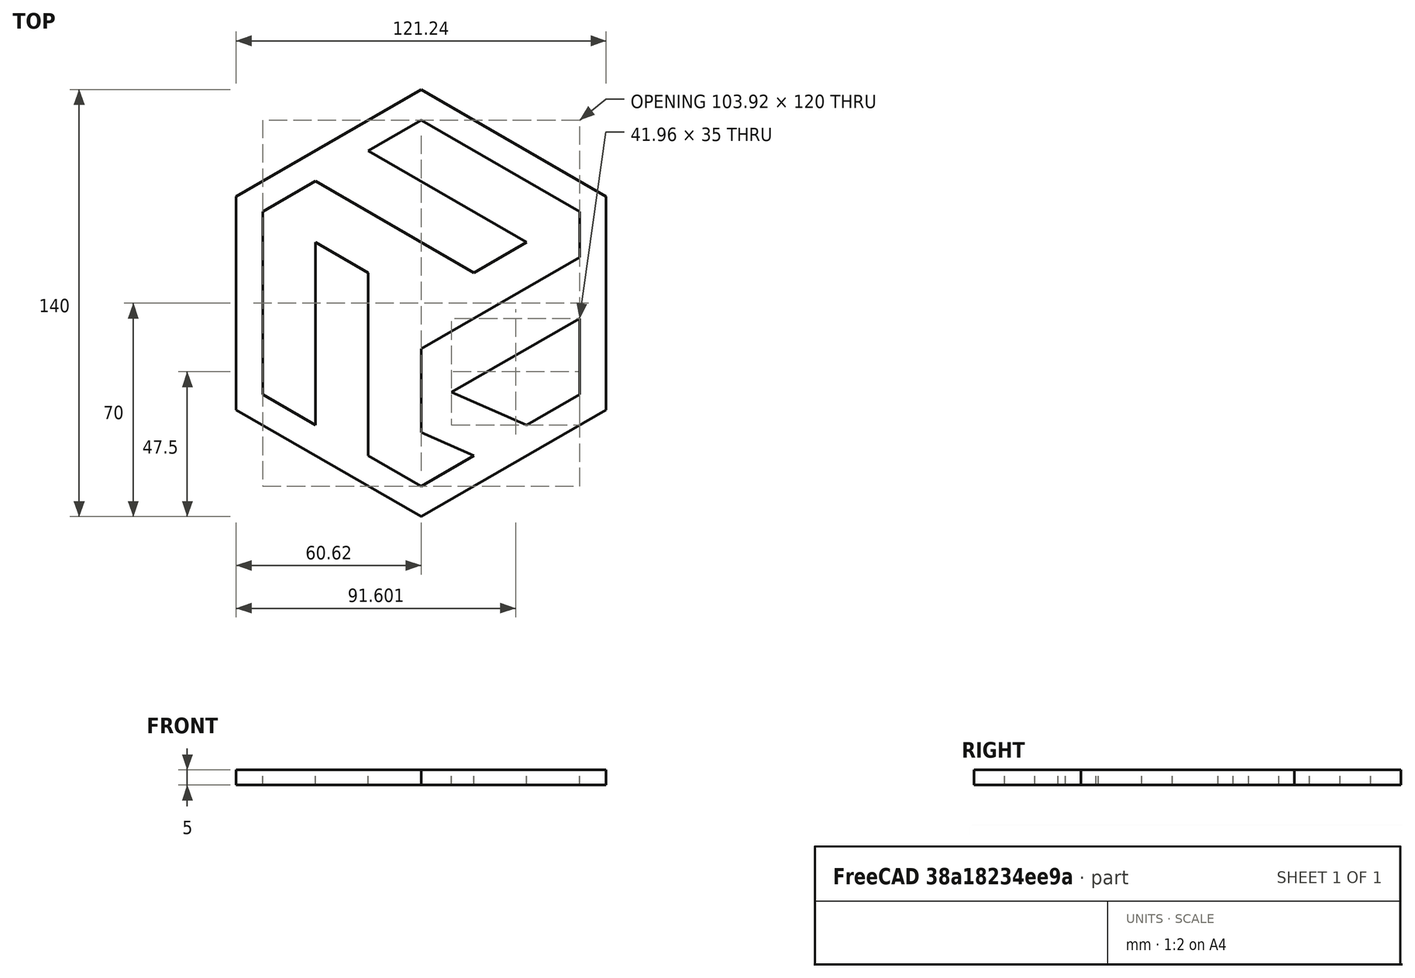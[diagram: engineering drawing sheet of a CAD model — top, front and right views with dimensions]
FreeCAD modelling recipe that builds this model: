
FCSTD DOCUMENT  (FreeCAD 0.20R29603 (Git))
Label: logo
License: All rights reserved
LicenseURL: http://en.wikipedia.org/wiki/All_rights_reserved
objects: Sketcher::SketchObject×1, PartDesign::Pad×1, PartDesign::Body×1
note: 4 computed .brp shape members not serialized (recipe doc carries the construction recipe); baked Part::Feature solids carry a one-line shape summary decoded from their .brp

FEATURE [Sketcher::SketchObject] Sketch
  FullyConstrained = true
  MapMode = 5
  Support = -> [XY_Plane]
  sketch-geometry (37):
    g0: LineSegment StartX=51.9615 StartY=-30 StartZ=0 EndX=51.9615 EndY=30 EndZ=0
    g1: LineSegment StartX=51.9615 StartY=30 StartZ=0 EndX=0 EndY=60 EndZ=0
    g2: LineSegment StartX=0 StartY=60 StartZ=0 EndX=-51.9615 EndY=30 EndZ=0
    g3: LineSegment StartX=-51.9615 StartY=30 StartZ=0 EndX=-51.9615 EndY=-30 EndZ=0
    g4: LineSegment StartX=-51.9615 StartY=-30 StartZ=0 EndX=7.1e-15 EndY=-60 EndZ=0
    g5: LineSegment StartX=5.2e-15 StartY=-60 StartZ=0 EndX=51.9615 EndY=-30 EndZ=0
    g6: Circle CenterX=0 CenterY=-7.1e-15 CenterZ=0 NormalX=0 NormalY=0 NormalZ=1 AngleXU=0 Radius=60
    g7: LineSegment StartX=-17.3205 StartY=50 StartZ=0 EndX=34.641 EndY=20 EndZ=0
    g8: LineSegment StartX=-34.641 StartY=40 StartZ=0 EndX=17.3205 EndY=10 EndZ=0
    g9: LineSegment StartX=17.3205 StartY=10 StartZ=0 EndX=34.641 EndY=20 EndZ=0
    g10: LineSegment StartX=-34.641 StartY=-40 StartZ=0 EndX=-34.641 EndY=20 EndZ=0
    g11: LineSegment StartX=-34.641 StartY=20 StartZ=0 EndX=-17.3205 EndY=10 EndZ=0
    g12: LineSegment StartX=-17.3205 StartY=10 StartZ=0 EndX=-17.3205 EndY=-50 EndZ=0
    g13: LineSegment StartX=51.9615 StartY=15 StartZ=0 EndX=0 EndY=-15 EndZ=0
    g14: LineSegment StartX=51.9615 StartY=-5 StartZ=0 EndX=10 EndY=-29.2265 EndZ=0
    g15: LineSegment StartX=10 StartY=-29.2265 StartZ=0 EndX=34.641 EndY=-40 EndZ=0
    g16: LineSegment StartX=0 StartY=-15 StartZ=0 EndX=0 EndY=-42.4272 EndZ=0
    g17: LineSegment StartX=0 StartY=-42.4272 StartZ=0 EndX=17.3205 EndY=-50 EndZ=0
    g18: LineSegment StartX=-51.9615 StartY=30 StartZ=0 EndX=0 EndY=-7.1e-15 EndZ=0
    g19: LineSegment StartX=51.9615 StartY=30 StartZ=0 EndX=0 EndY=-7.1e-15 EndZ=0
    g20: LineSegment StartX=60.6218 StartY=35 StartZ=0 EndX=-7.1e-15 EndY=70 EndZ=0
    g21: LineSegment StartX=-7.1e-15 StartY=70 StartZ=0 EndX=-60.6218 EndY=35 EndZ=0
    g22: LineSegment StartX=-60.6218 StartY=35 StartZ=0 EndX=-60.6218 EndY=-35 EndZ=0
    g23: LineSegment StartX=-60.6218 StartY=-35 StartZ=0 EndX=0 EndY=-70 EndZ=0
    g24: LineSegment StartX=0 StartY=-70 StartZ=0 EndX=60.6218 EndY=-35 EndZ=0
    g25: LineSegment StartX=60.6218 StartY=-35 StartZ=0 EndX=60.6218 EndY=35 EndZ=0
    g26: Circle CenterX=0 CenterY=-7.1e-15 CenterZ=0 NormalX=0 NormalY=0 NormalZ=1 AngleXU=0 Radius=70
    g27: LineSegment StartX=0 StartY=60 StartZ=0 EndX=-17.3205 EndY=50 EndZ=0
    g28: LineSegment StartX=-34.641 StartY=40 StartZ=0 EndX=-51.9615 EndY=30 EndZ=0
    g29: LineSegment StartX=-51.9615 StartY=30 StartZ=0 EndX=-51.9615 EndY=-30 EndZ=0
    g30: LineSegment StartX=-51.9615 StartY=-30 StartZ=0 EndX=-34.641 EndY=-40 EndZ=0
    g31: LineSegment StartX=-17.3205 StartY=-50 StartZ=0 EndX=3.6e-15 EndY=-60 EndZ=0
    g32: LineSegment StartX=5.2e-15 StartY=-60 StartZ=0 EndX=17.3205 EndY=-50 EndZ=0
    g33: LineSegment StartX=34.641 StartY=-40 StartZ=0 EndX=51.9615 EndY=-30 EndZ=0
    g34: LineSegment StartX=51.9615 StartY=-30 StartZ=0 EndX=51.9615 EndY=-5 EndZ=0
    g35: LineSegment StartX=51.9615 StartY=15 StartZ=0 EndX=51.9615 EndY=30 EndZ=0
    g36: LineSegment StartX=51.9615 StartY=30 StartZ=0 EndX=0 EndY=60 EndZ=0
  constraints (93):
    c: Coincident(g0,g1)
    c: Coincident(g1,g2)
    c: Coincident(g2,g3)
    c: Coincident(g3,g4)
    c: Coincident(g4,g5)
    c: Coincident(g5,g0)
    c: Equal(g0, g1-g5) x5
    c: PointOnObject(g0,g6)
    c: PointOnObject(g1,g6)
    c: PointOnObject(g2,g6)
    c: PointOnObject(g3,g6)
    c: PointOnObject(g4,g6)
    c: PointOnObject(g5,g6)
    c: Coincident(g6,g-1)
    c: Vertical(g3)
    c: Radius(g6) = 60
    c: PointOnObject(g7,g2)
    c: PointOnObject(g8,g2)
    c: Coincident(g9,g8)
    c: Coincident(g9,g7)
    c: PointOnObject(g10,g4)
    c: Vertical(g10)
    c: Coincident(g11,g10)
    c: Coincident(g12,g11)
    c: PointOnObject(g12,g4)
    c: Vertical(g12)
    c: PointOnObject(g13,g0)
    c: PointOnObject(g14,g0)
    c: Coincident(g15,g14)
    c: PointOnObject(g15,g5)
    c: Coincident(g16,g13)
    c: Vertical(g16)
    c: Coincident(g17,g16)
    c: PointOnObject(g17,g5)
    c: Distance(g7,g1) = 20
    c: Distance(g8,g2) = 20
    c: Distance(g10,g3) = 20
    c: Distance(g4,g12) = 20
    c: Parallel(g15,g17)
    c: DistanceY(g14,g13) = 20
    c: Parallel(g1,g7)
    c: Parallel(g7,g8)
    c: Parallel(g14,g5)
    c: Parallel(g5,g13)
    c: Distance(g15,g17) = 20
    c: DistanceY(g13,g0) = 15
    c: Distance(g17,g4) = 20
    c: PointOnObject(g13,g-2)
    c: DistanceX(g13,g14) = 10
    c: Coincident(g18,g2)
    c: Coincident(g18,g6)
    c: Coincident(g19,g0)
    c: Coincident(g19,g6)
    c: PointOnObject(g10,g18)
    c: PointOnObject(g11,g18)
    c: PointOnObject(g7,g19)
    c: PointOnObject(g8,g19)
    c: Coincident(g20,g21)
    c: Coincident(g21,g22)
    c: Coincident(g22,g23)
    c: Coincident(g23,g24)
    c: Coincident(g24,g25)
    c: Coincident(g25,g20)
    c: Equal(g20, g21-g25) x5
    c: PointOnObject(g20,g26)
    c: PointOnObject(g21,g26)
    c: PointOnObject(g22,g26)
    c: PointOnObject(g23,g26)
    c: PointOnObject(g24,g26)
    c: PointOnObject(g25,g26)
    c: Coincident(g26,g6)
    c: Radius(g26) = 70
    c: Vertical(g22)
    c: Coincident(g27,g1)
    c: Coincident(g27,g7)
    c: Coincident(g28,g8)
    c: Coincident(g28,g2)
    c: Coincident(g29,g28)
    c: Coincident(g29,g3)
    c: Coincident(g30,g29)
    c: Coincident(g30,g10)
    c: Coincident(g31,g12)
    c: Coincident(g31,g4)
    c: Coincident(g32,g31)
    c: Coincident(g32,g17)
    c: Coincident(g33,g15)
    c: Coincident(g33,g0)
    c: Coincident(g34,g33)
    c: Coincident(g34,g14)
    c: Coincident(g35,g13)
    c: Coincident(g35,g0)
    c: Coincident(g36,g35)
    c: Coincident(g36,g27)
FEATURE [PartDesign::Pad] Pad
  Direction = (0,0,1)
  Length = 5
  Length2 = 10
  Profile = -> Sketch
  ReferenceAxis = -> Sketch [N_Axis]
  Type = 0
FEATURE [PartDesign::Body] Body
  Group = -> [Sketch,Pad]
  Origin = -> Origin
  Tip = -> Pad
